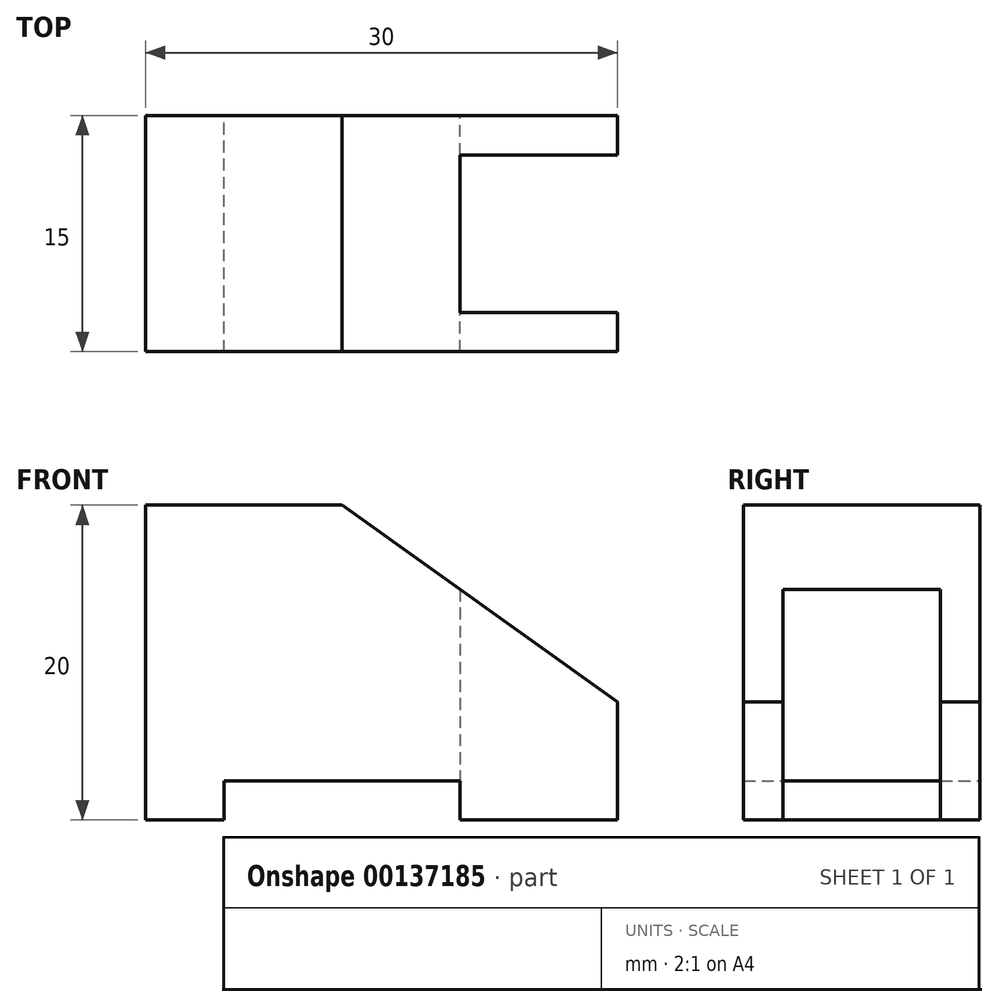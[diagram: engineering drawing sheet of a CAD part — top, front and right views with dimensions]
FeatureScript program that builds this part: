
annotation { "Feature Type Name" : "Feature", "Feature Type Description" : "" }
export const myFeature = defineFeature(function(context is Context, id is Id, definition is map)
    precondition{}
    {
        {
            var Q0;
            Q0=qCreatedBy(makeId("Front.planeOp"),FACE);
            var sketch = newSketch(context, id + "F0", { "sketchPlane" : qUnion([Q0])});
            skLineSegment(sketch, "E0", {"start": v(0, 20) * mm, "end": v(0, 0) * mm});
            skLineSegment(sketch, "E1", {"start": v(0, 0) * mm, "end": v(5, 0) * mm});
            skLineSegment(sketch, "E2", {"start": v(5, 0) * mm, "end": v(5, 2.5) * mm});
            skLineSegment(sketch, "E3", {"start": v(5, 2.5) * mm, "end": v(20, 2.5) * mm});
            skLineSegment(sketch, "E4", {"start": v(20, 2.5) * mm, "end": v(20, 0) * mm});
            skLineSegment(sketch, "E5", {"start": v(20, 0) * mm, "end": v(30, 0) * mm});
            skLineSegment(sketch, "E6", {"start": v(30, 0) * mm, "end": v(30, 7.5) * mm});
            skLineSegment(sketch, "E7", {"start": v(30, 7.5) * mm, "end": v(12.5, 20) * mm});
            skLineSegment(sketch, "E8", {"start": v(12.5, 20) * mm, "end": v(0, 20) * mm});
            skSolve(sketch);
        }
        {
            var Q0;
            Q0 = qSketchRegion(id + "F0", true);
            extrude(context, id + "F1", {"entities" : qUnion([Q0]), "depth" : 15 * mm});
        }
        {
            var Q0;
            Q0=qCreatedBy(makeId("Top.planeOp"),FACE);
            var sketch = newSketch(context, id + "F2", { "sketchPlane" : qUnion([Q0])});
            skLineSegment(sketch, "E9.bottom", {"start": v(20, -2.5) * mm, "end": v(30, -2.5) * mm});
            skLineSegment(sketch, "E9.top", {"start": v(20, -12.5) * mm, "end": v(30, -12.5) * mm});
            skLineSegment(sketch, "E9.left", {"start": v(20, -2.5) * mm, "end": v(20, -12.5) * mm});
            skLineSegment(sketch, "E9.right", {"start": v(30, -2.5) * mm, "end": v(30, -12.5) * mm});
            skSolve(sketch);
        }
        {
            var Q0;
            Q0 = qSketchRegion(id + "F2", true);
            extrude(context, id + "F3", {"entities" : qUnion([Q0]), "operationType" : NewBodyOperationType.REMOVE, "endBound" : BoundingType.THROUGH_ALL, "depth" : 25 * mm});
        }
    });
